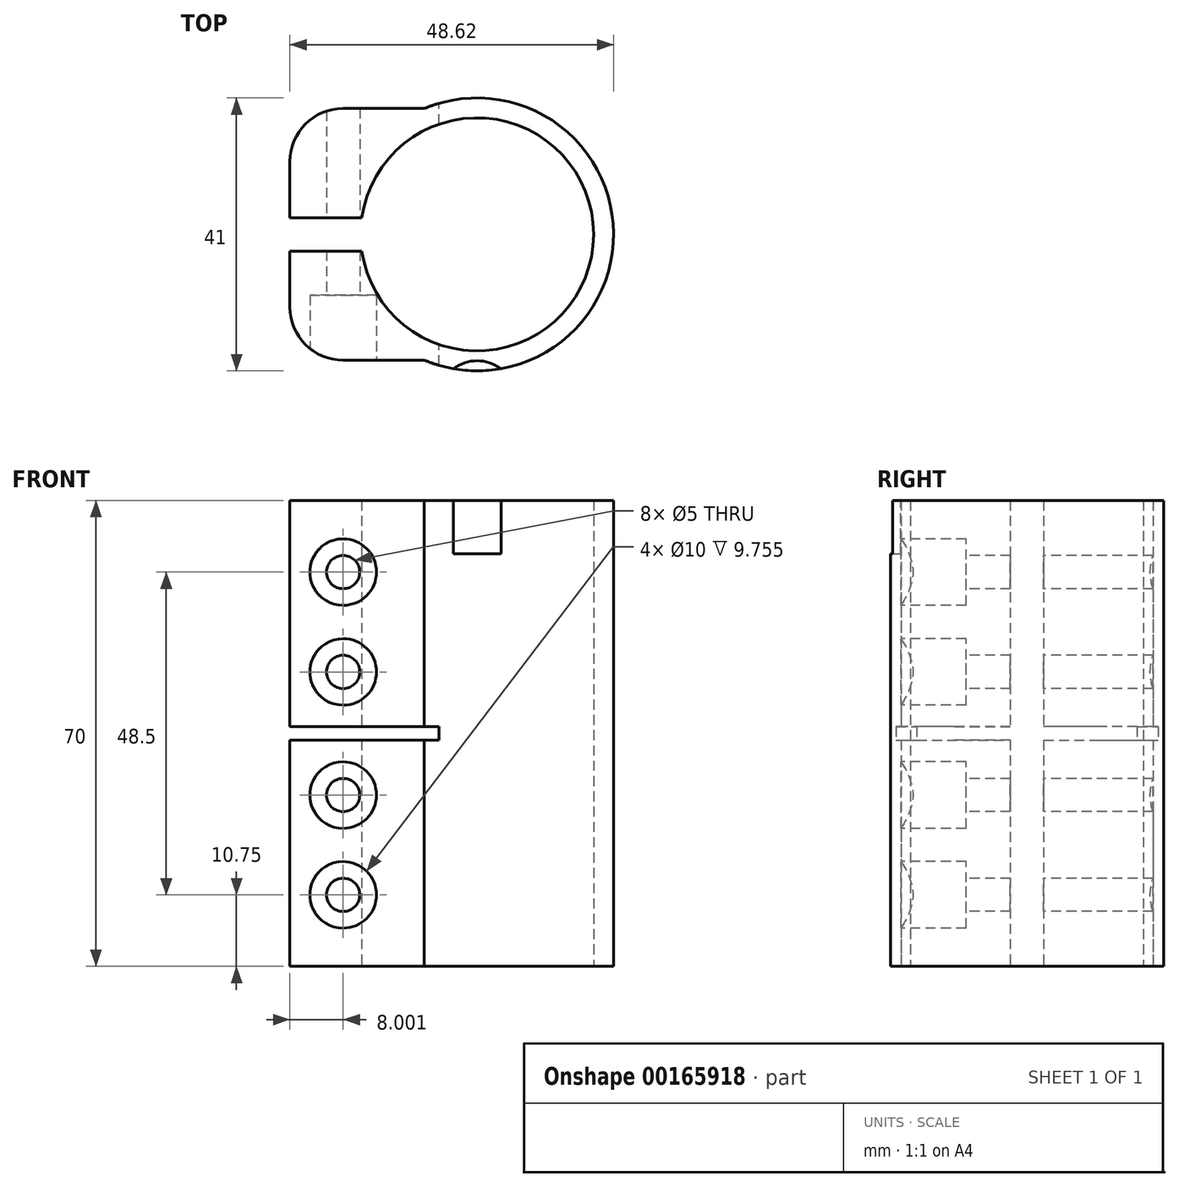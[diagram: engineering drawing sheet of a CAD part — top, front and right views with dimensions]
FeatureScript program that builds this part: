
annotation { "Feature Type Name" : "Feature", "Feature Type Description" : "" }
export const myFeature = defineFeature(function(context is Context, id is Id, definition is map)
    precondition{}
    {
        {
            var Q0;
            Q0=qCreatedBy(makeId("Top.planeOp"),FACE);
            var sketch = newSketch(context, id + "F0", { "sketchPlane" : qUnion([Q0])});
            skPoint(sketch, "E0", {"position": v(0, 0) * mm});
            skArc(sketch, "E1", {"start": v(-17.32, -2.5) * mm, "mid": v(17.5, 0) * mm, "end": v(-17.32, 2.5) * mm});
            skArc(sketch, "E2", {"start": v(-7.92, -18.9) * mm, "mid": v(20.5, 0) * mm, "end": v(-7.92, 18.9) * mm});
            skLineSegment(sketch, "E3", {"start": v(-7.92, 18.9) * mm, "end": v(-20.12, 18.9) * mm});
            skLineSegment(sketch, "E4", {"start": v(-28.12, 10.9) * mm, "end": v(-28.12, 2.5) * mm});
            skLineSegment(sketch, "E5", {"start": v(-28.12, 2.5) * mm, "end": v(-17.32, 2.5) * mm});
            skPoint(sketch, "E6.visualSharp", {"position": v(-28.12, 18.9) * mm});
            skArc(sketch, "E6.filletArc", {"start": v(-20.12, 18.9) * mm, "mid": v(-25.78, 16.57) * mm, "end": v(-28.12, 10.9) * mm});
            skLineSegment(sketch, "E7", {"start": v(0, 0) * mm, "end": v(48.76, 0) * mm, "construction": true});
            skLineSegment(sketch, "E8.MirrorCS", {"start": v(-7.92, -18.9) * mm, "end": v(-20.12, -18.9) * mm});
            skArc(sketch, "E9.MirrorCS", {"start": v(-20.12, -18.9) * mm, "mid": v(-25.78, -16.57) * mm, "end": v(-28.12, -10.9) * mm});
            skLineSegment(sketch, "E10.MirrorCS", {"start": v(-28.12, -10.9) * mm, "end": v(-28.12, -2.5) * mm});
            skLineSegment(sketch, "E11.MirrorCS", {"start": v(-28.12, -2.5) * mm, "end": v(-17.32, -2.5) * mm});
            skSolve(sketch);
        }
        {
            var Q0;
            Q0 = qSketchRegion(id + "F0", true);
            extrude(context, id + "F1", {"entities" : qUnion([Q0]), "endBound" : BoundingType.SYMMETRIC, "depth" : 70 * mm});
        }
        {
            var Q0;
            Q0=makeQuery(id+"F1.opExtrude","SWEPT_FACE",FACE,{"disambiguationData":[OSD([sQuery(id+"F0.wireOp",EDGE,"E8.MirrorCS")])]});
            var sketch = newSketch(context, id + "F2", { "sketchPlane" : qUnion([Q0])});
            skPoint(sketch, "E12", {"position": v(-20.12, -24.25) * mm});
            skPoint(sketch, "E13", {"position": v(-20.12, -9.25) * mm});
            skPoint(sketch, "E14", {"position": v(-20.12, 9.25) * mm});
            skPoint(sketch, "E15", {"position": v(-20.12, 24.25) * mm});
            skSolve(sketch);
        }
        {
            var Q0;
            Q0=sQuery(id+"F2.wireOp",VERTEX,"E12");
            var Q1;
            Q1=sQuery(id+"F2.wireOp",VERTEX,"E13");
            var Q2;
            Q2=sQuery(id+"F2.wireOp",VERTEX,"E14");
            var Q3;
            Q3=sQuery(id+"F2.wireOp",VERTEX,"E15");
            var Q4;
            Q4=makeQuery(id+"F1.opExtrude","SWEPT_BODY",BODY,{"disambiguationData":[OSD([sQuery(id+"F0.wireOp",EDGE,"E1"),sQuery(id+"F0.wireOp",EDGE,"E2"),sQuery(id+"F0.wireOp",EDGE,"E3"),sQuery(id+"F0.wireOp",EDGE,"E4"),sQuery(id+"F0.wireOp",EDGE,"E5"),sQuery(id+"F0.wireOp",EDGE,"E6.filletArc"),sQuery(id+"F0.wireOp",EDGE,"E8.MirrorCS"),sQuery(id+"F0.wireOp",EDGE,"E9.MirrorCS"),sQuery(id+"F0.wireOp",EDGE,"E10.MirrorCS"),sQuery(id+"F0.wireOp",EDGE,"E11.MirrorCS")])]});
            hole(context, id + "F3", {"style" : HoleStyle.C_BORE, "endStyle" : HoleEndStyle.THROUGH, "holeDiameter" : 5 * mm, "cBoreDiameter" : 10 * mm, "cBoreDepth" : 8 * mm, "locations" : qUnion([Q0, Q1, Q2, Q3]), "scope" : qUnion([Q4]), "isTappedThrough" : true});
        }
        {
            var Q0;
            Q0=qCreatedBy(makeId("Front.planeOp"),FACE);
            var sketch = newSketch(context, id + "F4", { "sketchPlane" : qUnion([Q0])});
            skLineSegment(sketch, "E16", {"start": v(-32.28, 1) * mm, "end": v(-5.72, 1) * mm});
            skLineSegment(sketch, "E17", {"start": v(-5.72, 1) * mm, "end": v(-5.72, -1) * mm});
            skLineSegment(sketch, "E18", {"start": v(-5.72, -1) * mm, "end": v(-32.28, -1) * mm});
            skLineSegment(sketch, "E19", {"start": v(-32.28, -1) * mm, "end": v(-32.28, 1) * mm});
            skSolve(sketch);
        }
        {
            var Q0;
            Q0 = qSketchRegion(id + "F4", true);
            extrude(context, id + "F5", {"entities" : qUnion([Q0]), "operationType" : NewBodyOperationType.REMOVE, "endBound" : BoundingType.SYMMETRIC, "depth" : 50 * mm});
        }
        {
            var Q0;
            Q0=makeQuery(id+"F1.opExtrude","CAP_FACE",FACE,{"disambiguationData":[OSD([sQuery(id+"F0.wireOp",EDGE,"E1"),sQuery(id+"F0.wireOp",EDGE,"E2"),sQuery(id+"F0.wireOp",EDGE,"E3"),sQuery(id+"F0.wireOp",EDGE,"E4"),sQuery(id+"F0.wireOp",EDGE,"E5"),sQuery(id+"F0.wireOp",EDGE,"E6.filletArc"),sQuery(id+"F0.wireOp",EDGE,"E8.MirrorCS"),sQuery(id+"F0.wireOp",EDGE,"E9.MirrorCS"),sQuery(id+"F0.wireOp",EDGE,"E10.MirrorCS"),sQuery(id+"F0.wireOp",EDGE,"E11.MirrorCS")])],"isStart":false});
            var sketch = newSketch(context, id + "F6", { "sketchPlane" : qUnion([Q0])});
            skPoint(sketch, "E20", {"position": v(0, -25) * mm});
            skCircle(sketch, "E21", {"center": v(0, -25) * mm, "radius": 6 * mm});
            skSolve(sketch);
        }
        {
            var Q0;
            {var subQ0=sQuery(id+"F6.wireOp",EDGE,"E21");var subQ1=makeQuery(id+"F1.opExtrude","CAP_EDGE",EDGE,{"disambiguationData":[OSD([sQuery(id+"F0.wireOp",EDGE,"E2")])],"isStart":false});var subQ2=makeQuery(id+"F6.imprint","INTERSECT",VERTEX,{"disambiguationData":[OD(0.0)],"derivedFrom":[subQ1,subQ0]});Q0=makeQuery(id+"F6.imprint","IMPRINT",FACE,{"disambiguationData":[TD([[makeQuery(id+"F6.imprint","IMPRINT",EDGE,{"disambiguationData":[TD([[subQ2,-1.0]])],"derivedFrom":subQ0}),1.0]])]});}
            var Q1;
            Q1=makeQuery(id+"FMo0qCXoM8Fg9h5_1.1.F6.imprint","IMPRINT",FACE,{"disambiguationData":[TD([[makeQuery(id+"FMo0qCXoM8Fg9h5_1.1.F6.imprint","IMPRINT",EDGE,{"derivedFrom":sQuery(id+"FMo0qCXoM8Fg9h5_1.1.F6.wireOp",EDGE,"E21")}),1.0]])]});
            var Q2;
            Q2=makeQuery(id+"FMo0qCXoM8Fg9h5_1.2.F6.imprint","IMPRINT",FACE,{"disambiguationData":[TD([[makeQuery(id+"FMo0qCXoM8Fg9h5_1.2.F6.imprint","IMPRINT",EDGE,{"derivedFrom":sQuery(id+"FMo0qCXoM8Fg9h5_1.2.F6.wireOp",EDGE,"E21")}),1.0]])]});
            var Q3;
            Q3=makeQuery(id+"FMo0qCXoM8Fg9h5_1.3.F6.imprint","IMPRINT",FACE,{"disambiguationData":[TD([[makeQuery(id+"FMo0qCXoM8Fg9h5_1.3.F6.imprint","IMPRINT",EDGE,{"derivedFrom":sQuery(id+"FMo0qCXoM8Fg9h5_1.3.F6.wireOp",EDGE,"E21")}),1.0]])]});
            var Q4;
            Q4=makeQuery(id+"FMo0qCXoM8Fg9h5_1.4.F6.imprint","IMPRINT",FACE,{"disambiguationData":[TD([[makeQuery(id+"FMo0qCXoM8Fg9h5_1.4.F6.imprint","IMPRINT",EDGE,{"derivedFrom":sQuery(id+"FMo0qCXoM8Fg9h5_1.4.F6.wireOp",EDGE,"E21")}),1.0]])]});
            extrude(context, id + "F7", {"entities" : qUnion([Q0, Q1, Q2, Q3, Q4]), "operationType" : NewBodyOperationType.REMOVE, "oppositeDirection" : true, "depth" : 8 * mm});
        }
        {
            var Q0;
            Q0 = qSketchRegion(id + "F6", true);
            extrude(context, id + "F8", {"entities" : qUnion([Q0]), "operationType" : NewBodyOperationType.REMOVE, "oppositeDirection" : true, "depth" : 8 * mm});
        }
    });
